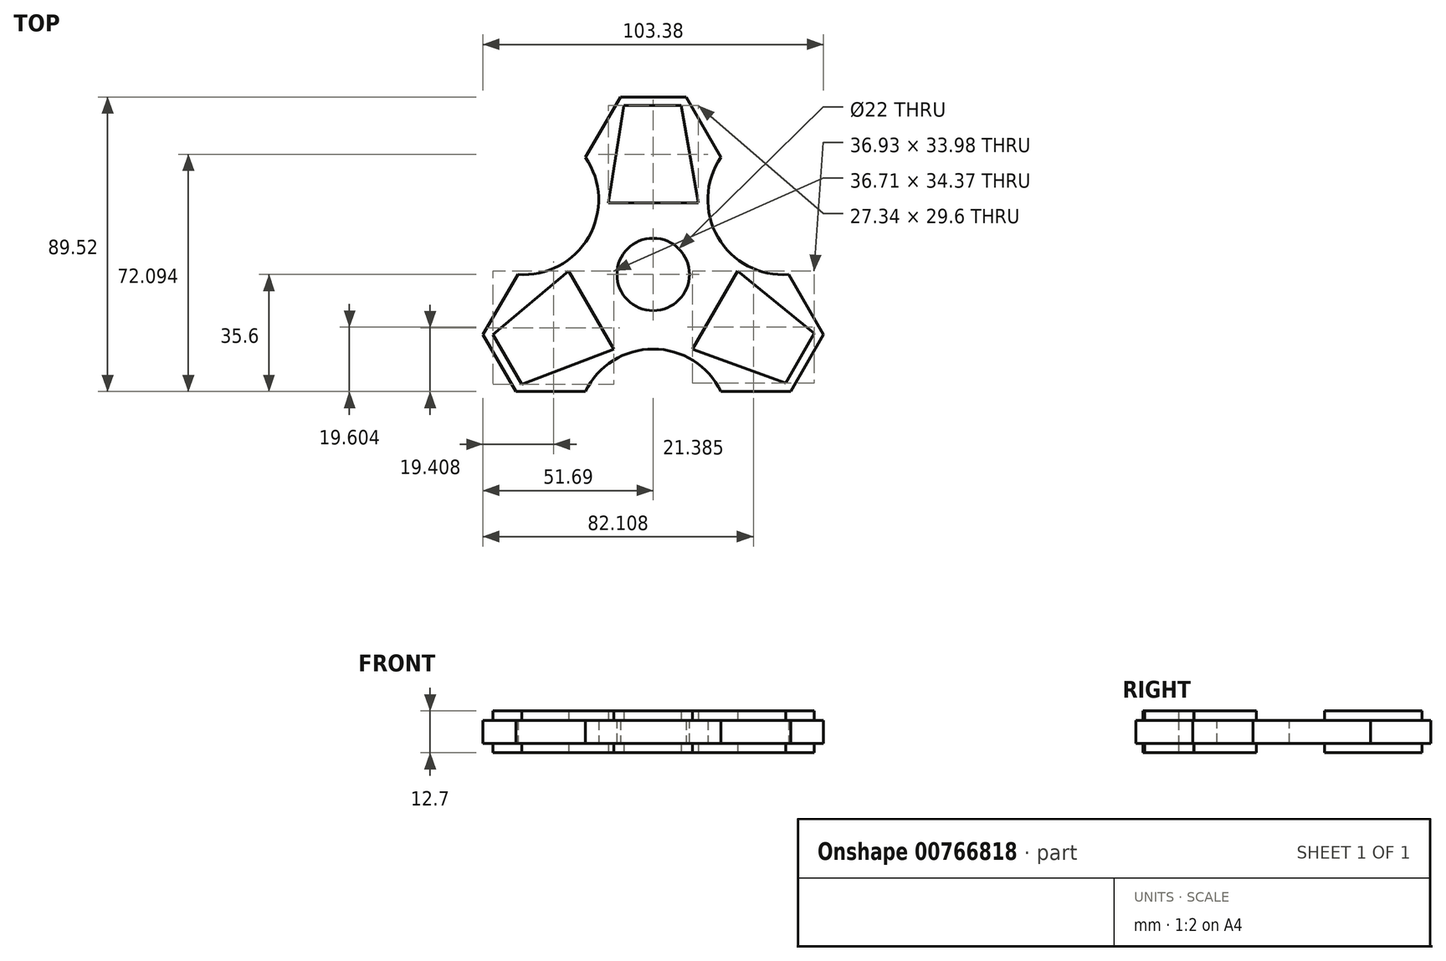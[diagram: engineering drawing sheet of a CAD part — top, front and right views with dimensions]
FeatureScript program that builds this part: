
annotation { "Feature Type Name" : "Feature", "Feature Type Description" : "" }
export const myFeature = defineFeature(function(context is Context, id is Id, definition is map)
    precondition{}
    {
        {
            var Q0;
            Q0=qCreatedBy(makeId("Top.planeOp"),FACE);
            var sketch = newSketch(context, id + "F0", { "sketchPlane" : qUnion([Q0])});
            skLineSegment(sketch, "E0.0", {"start": v(41.71, -35.6) * mm, "end": v(20.55, -35.6) * mm});
            skLineSegment(sketch, "E0.1", {"start": v(-51.69, -18.33) * mm, "end": v(-41.1, 0) * mm});
            skLineSegment(sketch, "E0.2", {"start": v(9.97, 53.92) * mm, "end": v(20.55, 35.6) * mm});
            skPoint(sketch, "E0.0.midPoint", {"position": v(0, -35.6) * mm});
            skLineSegment(sketch, "E1", {"start": v(-9.97, 53.92) * mm, "end": v(9.97, 53.92) * mm});
            skLineSegment(sketch, "E2.1.0", {"start": v(51.69, -18.33) * mm, "end": v(41.71, -35.6) * mm});
            skLineSegment(sketch, "E2.2.0", {"start": v(-41.71, -35.6) * mm, "end": v(-51.69, -18.33) * mm});
            skPoint(sketch, "E2.center", {"position": v(0, 0) * mm});
            skLineSegment(sketch, "E2.anchor1", {"start": v(0, 0) * mm, "end": v(-9.97, 53.92) * mm, "construction": true});
            skLineSegment(sketch, "E2.anchor2", {"start": v(0, 0) * mm, "end": v(-41.71, -35.6) * mm, "construction": true});
            skPoint(sketch, "E3.orphan", {"position": v(61.66, -35.6) * mm});
            skPoint(sketch, "E4.orphan", {"position": v(-61.66, -35.6) * mm});
            skArc(sketch, "E5", {"start": v(-41.1, 0) * mm, "mid": v(-19.63, 11.33) * mm, "end": v(-20.55, 35.6) * mm});
            skArc(sketch, "E6.1.0", {"start": v(20.55, -35.6) * mm, "mid": v(0, -22.66) * mm, "end": v(-20.55, -35.6) * mm});
            skArc(sketch, "E6.2.0", {"start": v(20.55, 35.6) * mm, "mid": v(19.63, 11.33) * mm, "end": v(41.1, 0) * mm});
            skLineSegment(sketch, "E7.trimOffspring", {"start": v(-20.55, 35.6) * mm, "end": v(-9.97, 53.92) * mm});
            skLineSegment(sketch, "E8.trimOffspring", {"start": v(41.1, 0) * mm, "end": v(51.69, -18.33) * mm});
            skLineSegment(sketch, "E9.trimOffspring", {"start": v(-20.55, -35.6) * mm, "end": v(-41.71, -35.6) * mm});
            skPoint(sketch, "E10", {"position": v(-46.7, -26.96) * mm});
            skSolve(sketch);
        }
        {
            var Q0;
            Q0 = qSketchRegion(id + "F0", true);
            extrude(context, id + "F1", {"entities" : qUnion([Q0]), "endBound" : BoundingType.SYMMETRIC, "depth" : 7 * mm, "offsetDistance" : 25 * mm});
        }
        {
            var Q0;
            Q0=makeQuery(id+"F1.opExtrude","CAP_FACE",FACE,{"disambiguationData":[OSD([sQuery(id+"F0.wireOp",EDGE,"E0.0"),sQuery(id+"F0.wireOp",EDGE,"E0.1"),sQuery(id+"F0.wireOp",EDGE,"E0.2"),sQuery(id+"F0.wireOp",EDGE,"E1"),sQuery(id+"F0.wireOp",EDGE,"E2.1.0"),sQuery(id+"F0.wireOp",EDGE,"E2.2.0"),sQuery(id+"F0.wireOp",EDGE,"E5"),sQuery(id+"F0.wireOp",EDGE,"E6.1.0"),sQuery(id+"F0.wireOp",EDGE,"E6.2.0"),sQuery(id+"F0.wireOp",EDGE,"E7.trimOffspring"),sQuery(id+"F0.wireOp",EDGE,"E8.trimOffspring"),sQuery(id+"F0.wireOp",EDGE,"E9.trimOffspring")])],"isStart":false});
            var sketch = newSketch(context, id + "F2", { "sketchPlane" : qUnion([Q0])});
            skCircle(sketch, "E11", {"center": v(0, 0) * mm, "radius": 11 * mm});
            skSolve(sketch);
        }
        {
            var Q0;
            Q0 = qSketchRegion(id + "F2", true);
            extrude(context, id + "F3", {"entities" : qUnion([Q0]), "operationType" : NewBodyOperationType.REMOVE, "oppositeDirection" : true, "depth" : 63.5 * mm, "offsetDistance" : 25 * mm});
        }
        {
            var Q0;
            Q0=qCreatedBy(makeId("Top.planeOp"),FACE);
            var sketch = newSketch(context, id + "F4", { "sketchPlane" : qUnion([Q0])});
            skLineSegment(sketch, "E12", {"start": v(-8.93, 51.3) * mm, "end": v(8.47, 51.3) * mm});
            skLineSegment(sketch, "E13", {"start": v(13.67, 21.7) * mm, "end": v(-13.67, 21.7) * mm});
            skLineSegment(sketch, "E14", {"start": v(-13.67, 21.7) * mm, "end": v(-8.93, 51.3) * mm});
            skLineSegment(sketch, "E15", {"start": v(8.47, 51.3) * mm, "end": v(13.67, 21.7) * mm});
            skLineSegment(sketch, "E16.1.0", {"start": v(-25.62, 1) * mm, "end": v(-11.95, -22.69) * mm});
            skLineSegment(sketch, "E16.2.0", {"start": v(11.95, -22.69) * mm, "end": v(25.62, 1) * mm});
            skPoint(sketch, "E16.center", {"position": v(0, 0) * mm});
            skLineSegment(sketch, "E17.1.0", {"start": v(-39.96, -33.38) * mm, "end": v(-48.66, -18.3) * mm});
            skLineSegment(sketch, "E17.2.0", {"start": v(48.89, -17.92) * mm, "end": v(40.19, -32.99) * mm});
            skLineSegment(sketch, "E18.1.0", {"start": v(-11.95, -22.69) * mm, "end": v(-39.96, -33.38) * mm});
            skLineSegment(sketch, "E18.2.0", {"start": v(25.62, 1) * mm, "end": v(48.89, -17.92) * mm});
            skLineSegment(sketch, "E19.1.0", {"start": v(-48.66, -18.3) * mm, "end": v(-25.62, 1) * mm});
            skLineSegment(sketch, "E19.2.0", {"start": v(40.19, -32.99) * mm, "end": v(11.95, -22.69) * mm});
            skSolve(sketch);
        }
        {
            var Q0;
            Q0 = qSketchRegion(id + "F4", true);
            extrude(context, id + "F5", {"entities" : qUnion([Q0]), "operationType" : NewBodyOperationType.ADD, "endBound" : BoundingType.SYMMETRIC, "depth" : 12.7 * mm, "offsetDistance" : 25 * mm});
        }
    });
